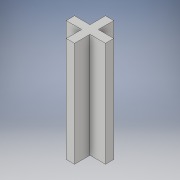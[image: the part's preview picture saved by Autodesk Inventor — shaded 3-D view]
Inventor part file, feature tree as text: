
AUTODESK INVENTOR PART (.ipt)
format: ipt  version: 2019 (Build 230136000, 136)  size: 101,376 bytes
history: native  units: mm
features: extrude x1, sketch x1
ambient origin geometry x8: Origin, YZ Plane, XZ Plane, XY Plane, X Axis, Y Axis, Z Axis, Center Point
bodies: Solid1 (feature_tree)
feature tree (2):
  extrude  "Extrusion1"  Depth=3.18mm
  sketch  "Sketch1"  dims[d0=15.0mm d1=3.18mm d2=3.18mm d3=15.0mm d4=40.0mm d5=0.0mm]
